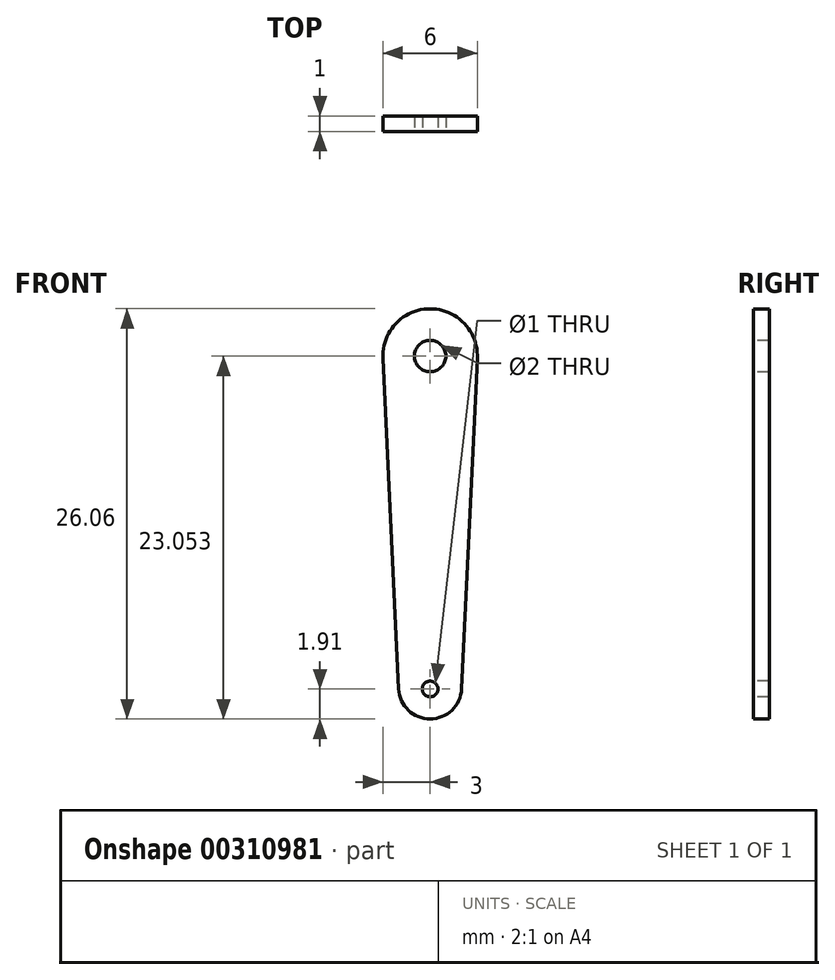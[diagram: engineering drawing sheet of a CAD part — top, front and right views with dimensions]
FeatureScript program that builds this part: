
annotation { "Feature Type Name" : "Feature", "Feature Type Description" : "" }
export const myFeature = defineFeature(function(context is Context, id is Id, definition is map)
    precondition{}
    {
        {
            var Q0;
            Q0=qCreatedBy(makeId("Front.planeOp"),FACE);
            var sketch = newSketch(context, id + "F0", { "sketchPlane" : qUnion([Q0])});
            skLineSegment(sketch, "E0", {"start": v(-2, 0) * mm, "end": v(2, 0) * mm});
            skLineSegment(sketch, "E1", {"start": v(2, 0) * mm, "end": v(3, 21) * mm});
            skLineSegment(sketch, "E2", {"start": v(3, 21) * mm, "end": v(-3, 21) * mm});
            skLineSegment(sketch, "E3", {"start": v(-3, 21) * mm, "end": v(-2, 0) * mm});
            skArc(sketch, "E4", {"start": v(-2, 0) * mm, "mid": v(0, -1.9) * mm, "end": v(2, 0) * mm});
            skArc(sketch, "E5", {"start": v(3, 21) * mm, "mid": v(0, 24.15) * mm, "end": v(-3, 21) * mm});
            skSolve(sketch);
        }
        {
            var Q0;
            Q0=makeQuery(id+"F0.imprint","IMPRINT",FACE,{"disambiguationData":[TD([[makeQuery(id+"F0.imprint","IMPRINT",EDGE,{"derivedFrom":sQuery(id+"F0.wireOp",EDGE,"E0")}),1.0]])]});
            var Q1;
            Q1=makeQuery(id+"F0.imprint","IMPRINT",FACE,{"disambiguationData":[TD([[makeQuery(id+"F0.imprint","IMPRINT",EDGE,{"derivedFrom":sQuery(id+"F0.wireOp",EDGE,"E2")}),-1.0]])]});
            var Q2;
            Q2=makeQuery(id+"F0.imprint","IMPRINT",FACE,{"disambiguationData":[TD([[makeQuery(id+"F0.imprint","IMPRINT",EDGE,{"derivedFrom":sQuery(id+"F0.wireOp",EDGE,"E0")}),-1.0]])]});
            extrude(context, id + "F1", {"entities" : qUnion([Q0, Q1, Q2]), "depth" : 1 * mm});
        }
        {
            var Q0;
            Q0=makeQuery(id+"F1.opExtrude","CAP_FACE",FACE,{"disambiguationData":[OSD([sQuery(id+"F0.wireOp",EDGE,"E1"),sQuery(id+"F0.wireOp",EDGE,"E3"),sQuery(id+"F0.wireOp",EDGE,"E4"),sQuery(id+"F0.wireOp",EDGE,"E5")])],"isStart":false});
            var sketch = newSketch(context, id + "F2", { "sketchPlane" : qUnion([Q0])});
            skCircle(sketch, "E6", {"center": v(0, 0) * mm, "radius": 0.5 * mm});
            skCircle(sketch, "E7", {"center": v(0, 21.14) * mm, "radius": 1 * mm});
            skSolve(sketch);
        }
        {
            var Q0;
            Q0=makeQuery(id+"F2.imprint","IMPRINT",FACE,{"disambiguationData":[TD([[makeQuery(id+"F2.imprint","IMPRINT",EDGE,{"derivedFrom":sQuery(id+"F2.wireOp",EDGE,"E7")}),1.0]])]});
            var Q1;
            Q1=makeQuery(id+"F2.imprint","IMPRINT",FACE,{"disambiguationData":[TD([[makeQuery(id+"F2.imprint","IMPRINT",EDGE,{"derivedFrom":sQuery(id+"F2.wireOp",EDGE,"E6")}),1.0]])]});
            extrude(context, id + "F3", {"entities" : qUnion([Q0, Q1]), "operationType" : NewBodyOperationType.REMOVE, "endBound" : BoundingType.THROUGH_ALL, "oppositeDirection" : true, "depth" : 25 * mm});
        }
    });
